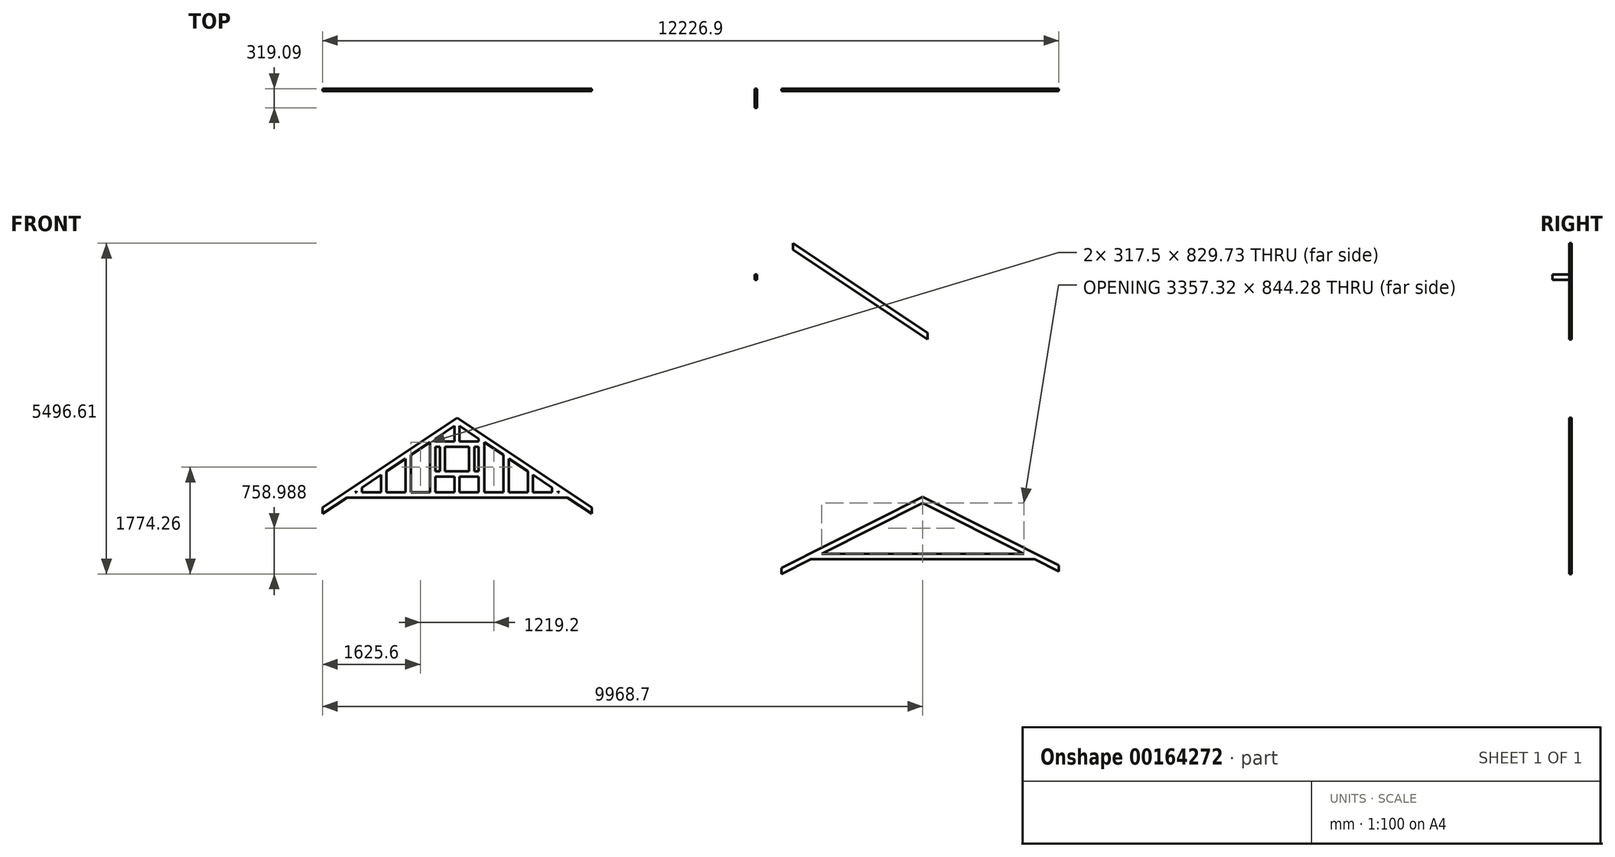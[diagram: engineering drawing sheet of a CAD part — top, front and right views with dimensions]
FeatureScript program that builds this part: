
annotation { "Feature Type Name" : "Feature", "Feature Type Description" : "" }
export const myFeature = defineFeature(function(context is Context, id is Id, definition is map)
    precondition{}
    {
        {
            var Q0;
            Q0=qCreatedBy(makeId("Front.planeOp"),FACE);
            var sketch = newSketch(context, id + "F0", { "sketchPlane" : qUnion([Q0])});
            skLineSegment(sketch, "E0.bottom", {"start": v(-99.94, 105.79) * mm, "end": v(3610.9, 105.79) * mm});
            skLineSegment(sketch, "E1", {"start": v(-592.94, -142.16) * mm, "end": v(-99.94, 105.79) * mm});
            skLineSegment(sketch, "E2", {"start": v(4013.66, -96.78) * mm, "end": v(3610.9, 105.79) * mm});
            skLineSegment(sketch, "E3", {"start": v(1738.69, 194.69) * mm, "end": v(76.82, 194.69) * mm});
            skLineSegment(sketch, "E4", {"start": v(1738.69, 194.69) * mm, "end": v(3434.14, 194.69) * mm});
            skLineSegment(sketch, "E5", {"start": v(-592.94, -42.65) * mm, "end": v(1755.48, 1138.48) * mm});
            skLineSegment(sketch, "E6", {"start": v(4013.66, 2.73) * mm, "end": v(1755.48, 1138.48) * mm});
            skLineSegment(sketch, "E7", {"start": v(-99.94, 105.79) * mm, "end": v(-592.94, -142.16) * mm});
            skLineSegment(sketch, "E8", {"start": v(3610.9, 105.79) * mm, "end": v(4013.66, -96.78) * mm});
            skLineSegment(sketch, "E9", {"start": v(-592.94, -42.65) * mm, "end": v(-592.94, -142.16) * mm});
            skLineSegment(sketch, "E10", {"start": v(4013.66, 2.73) * mm, "end": v(4013.66, -96.78) * mm});
            skLineSegment(sketch, "E11.trimOffspring", {"start": v(76.82, 194.69) * mm, "end": v(1755.48, 1038.97) * mm});
            skLineSegment(sketch, "E12.trimOffspring", {"start": v(3434.14, 194.69) * mm, "end": v(1755.48, 1038.97) * mm});
            skSolve(sketch);
        }
        {
            var Q0;
            Q0 = qSketchRegion(id + "F0", true);
            extrude(context, id + "F1", {"entities" : qUnion([Q0]), "depth" : 38.1 * mm});
        }
        {
            var Q0;
            Q0=qCreatedBy(makeId("Front.planeOp"),FACE);
            var sketch = newSketch(context, id + "F2", { "sketchPlane" : qUnion([Q0])});
            skLineSegment(sketch, "E13.bottom", {"start": v(-7806.82, 1128.33) * mm, "end": v(-4149.22, 1128.33) * mm});
            skPoint(sketch, "E14.endSnap0", {"position": v(-5978.02, 1128.33) * mm});
            skLineSegment(sketch, "E15", {"start": v(-3742.82, 857.4) * mm, "end": v(-4149.22, 1128.33) * mm});
            skLineSegment(sketch, "E16", {"start": v(-6022.47, 1217.23) * mm, "end": v(-6339.97, 1217.23) * mm});
            skLineSegment(sketch, "E17", {"start": v(-5933.57, 1217.23) * mm, "end": v(-5616.07, 1217.23) * mm});
            skLineSegment(sketch, "E18", {"start": v(-8213.22, 964.24) * mm, "end": v(-5978.02, 2454.38) * mm});
            skLineSegment(sketch, "E19", {"start": v(-3742.82, 964.24) * mm, "end": v(-5978.02, 2454.38) * mm});
            skPoint(sketch, "E20.start.orphan", {"position": v(-6892.42, 1737.93) * mm});
            skPoint(sketch, "E21.start.orphan", {"position": v(-5063.62, 1737.93) * mm});
            skLineSegment(sketch, "E22", {"start": v(-7806.82, 1128.33) * mm, "end": v(-8213.22, 857.4) * mm});
            skLineSegment(sketch, "E23", {"start": v(-4149.22, 1128.33) * mm, "end": v(-3742.82, 857.4) * mm});
            skLineSegment(sketch, "E24.0", {"start": v(-5933.57, 1217.23) * mm, "end": v(-5933.57, 1475.46) * mm});
            skLineSegment(sketch, "E25.0", {"start": v(-6022.47, 1217.23) * mm, "end": v(-6022.47, 1475.46) * mm});
            skLineSegment(sketch, "E26.1.0.0", {"start": v(-6428.87, 1217.23) * mm, "end": v(-6428.87, 2046.96) * mm});
            skLineSegment(sketch, "E26.1.0.1", {"start": v(-6339.97, 1217.23) * mm, "end": v(-6339.97, 1475.46) * mm});
            skLineSegment(sketch, "E26.1.0.2", {"start": v(-6339.97, 1217.23) * mm, "end": v(-6022.47, 1217.23) * mm});
            skLineSegment(sketch, "E26.2.0.0", {"start": v(-6835.27, 1217.23) * mm, "end": v(-6835.27, 1776.03) * mm});
            skLineSegment(sketch, "E26.2.0.1", {"start": v(-6746.37, 1217.23) * mm, "end": v(-6746.37, 1835.3) * mm});
            skLineSegment(sketch, "E26.2.0.2", {"start": v(-6746.37, 1217.23) * mm, "end": v(-6428.87, 1217.23) * mm});
            skLineSegment(sketch, "E26.3.0.0", {"start": v(-7241.67, 1217.23) * mm, "end": v(-7241.67, 1505.1) * mm});
            skLineSegment(sketch, "E26.3.0.1", {"start": v(-7152.77, 1217.23) * mm, "end": v(-7152.77, 1564.36) * mm});
            skLineSegment(sketch, "E26.3.0.2", {"start": v(-7152.77, 1217.23) * mm, "end": v(-6835.27, 1217.23) * mm});
            skLineSegment(sketch, "E26.4.0.0", {"start": v(-7648.07, 1217.23) * mm, "end": v(-7648.07, 1234.16) * mm});
            skLineSegment(sketch, "E26.4.0.1", {"start": v(-7559.17, 1217.23) * mm, "end": v(-7559.17, 1293.43) * mm});
            skLineSegment(sketch, "E26.4.0.2", {"start": v(-7559.17, 1217.23) * mm, "end": v(-7241.67, 1217.23) * mm});
            skLineSegment(sketch, "E27.1.0.0", {"start": v(-5616.07, 1217.23) * mm, "end": v(-5616.07, 1475.46) * mm});
            skLineSegment(sketch, "E27.1.0.1", {"start": v(-5527.17, 1217.23) * mm, "end": v(-5527.17, 2046.96) * mm});
            skLineSegment(sketch, "E27.2.0.0", {"start": v(-5209.67, 1217.23) * mm, "end": v(-5209.67, 1835.3) * mm});
            skLineSegment(sketch, "E27.2.0.1", {"start": v(-5120.77, 1217.23) * mm, "end": v(-5120.77, 1776.03) * mm});
            skLineSegment(sketch, "E27.3.0.0", {"start": v(-4803.27, 1217.23) * mm, "end": v(-4803.27, 1564.36) * mm});
            skLineSegment(sketch, "E27.3.0.1", {"start": v(-4714.37, 1217.23) * mm, "end": v(-4714.37, 1505.1) * mm});
            skLineSegment(sketch, "E27.4.0.0", {"start": v(-4396.87, 1217.23) * mm, "end": v(-4396.87, 1293.43) * mm});
            skLineSegment(sketch, "E27.4.0.1", {"start": v(-4307.97, 1217.23) * mm, "end": v(-4307.97, 1234.16) * mm});
            skPoint(sketch, "E28.orphan", {"position": v(-6022.47, 2347.53) * mm});
            skPoint(sketch, "E29.orphan", {"position": v(-5933.57, 2347.53) * mm});
            skLineSegment(sketch, "E30", {"start": v(-5616.07, 1970.76) * mm, "end": v(-5692.27, 1970.76) * mm});
            skLineSegment(sketch, "E31", {"start": v(-5616.07, 1767.56) * mm, "end": v(-5616.07, 1564.36) * mm});
            skLineSegment(sketch, "E32", {"start": v(-5616.07, 1564.36) * mm, "end": v(-5692.27, 1564.36) * mm});
            skLineSegment(sketch, "E33.0", {"start": v(-5616.07, 1475.46) * mm, "end": v(-5933.57, 1475.46) * mm});
            skLineSegment(sketch, "E34.0", {"start": v(-5616.07, 2059.66) * mm, "end": v(-6339.97, 2059.66) * mm});
            skLineSegment(sketch, "E35.trimOffspring", {"start": v(-5692.27, 1564.36) * mm, "end": v(-5692.27, 1970.76) * mm});
            skLineSegment(sketch, "E36.trimOffspring", {"start": v(-6263.77, 1564.36) * mm, "end": v(-6263.77, 1970.76) * mm});
            skLineSegment(sketch, "E37.trimOffspring", {"start": v(-5933.57, 2059.66) * mm, "end": v(-5933.57, 2317.9) * mm});
            skLineSegment(sketch, "E38.trimOffspring", {"start": v(-6022.47, 2059.66) * mm, "end": v(-6022.47, 2317.9) * mm});
            skLineSegment(sketch, "E39.trimOffspring", {"start": v(-6746.37, 1835.3) * mm, "end": v(-6428.87, 2046.96) * mm});
            skLineSegment(sketch, "E40.trimOffspring", {"start": v(-7152.77, 1564.36) * mm, "end": v(-6835.27, 1776.03) * mm});
            skLineSegment(sketch, "E41.trimOffspring", {"start": v(-7559.17, 1293.43) * mm, "end": v(-7241.67, 1505.1) * mm});
            skLineSegment(sketch, "E42.trimOffspring", {"start": v(-7648.07, 1217.23) * mm, "end": v(-7673.47, 1217.23) * mm});
            skLineSegment(sketch, "E43.trimOffspring", {"start": v(-7241.67, 1217.23) * mm, "end": v(-7559.17, 1217.23) * mm});
            skLineSegment(sketch, "E44.trimOffspring", {"start": v(-6835.27, 1217.23) * mm, "end": v(-7152.77, 1217.23) * mm});
            skLineSegment(sketch, "E45.trimOffspring", {"start": v(-6428.87, 1217.23) * mm, "end": v(-6746.37, 1217.23) * mm});
            skLineSegment(sketch, "E46.trimOffspring", {"start": v(-5933.57, 1217.23) * mm, "end": v(-5908.17, 1217.23) * mm});
            skLineSegment(sketch, "E47.trimOffspring", {"start": v(-6022.47, 1475.46) * mm, "end": v(-6339.97, 1475.46) * mm});
            skLineSegment(sketch, "E48.trimOffspring", {"start": v(-6263.77, 1564.36) * mm, "end": v(-6339.97, 1564.36) * mm});
            skLineSegment(sketch, "E49.trimOffspring", {"start": v(-5781.17, 1564.36) * mm, "end": v(-6174.87, 1564.36) * mm});
            skLineSegment(sketch, "E50.trimOffspring", {"start": v(-5616.07, 1564.36) * mm, "end": v(-5616.07, 1970.76) * mm});
            skLineSegment(sketch, "E51.trimOffspring", {"start": v(-6339.97, 1564.36) * mm, "end": v(-6339.97, 1970.76) * mm});
            skLineSegment(sketch, "E52.trimOffspring", {"start": v(-5527.17, 1217.23) * mm, "end": v(-5209.67, 1217.23) * mm});
            skLineSegment(sketch, "E53.trimOffspring", {"start": v(-5527.17, 1217.23) * mm, "end": v(-5501.77, 1217.23) * mm});
            skLineSegment(sketch, "E54.trimOffspring", {"start": v(-5120.77, 1217.23) * mm, "end": v(-4803.27, 1217.23) * mm});
            skLineSegment(sketch, "E55.trimOffspring", {"start": v(-5120.77, 1217.23) * mm, "end": v(-5095.37, 1217.23) * mm});
            skLineSegment(sketch, "E56.trimOffspring", {"start": v(-4714.37, 1217.23) * mm, "end": v(-4688.97, 1217.23) * mm});
            skLineSegment(sketch, "E57.trimOffspring", {"start": v(-4714.37, 1217.23) * mm, "end": v(-4396.87, 1217.23) * mm});
            skLineSegment(sketch, "E58.trimOffspring", {"start": v(-4307.97, 1217.23) * mm, "end": v(-4282.57, 1217.23) * mm});
            skLineSegment(sketch, "E59.trimOffspring", {"start": v(-4396.87, 1293.43) * mm, "end": v(-4714.37, 1505.1) * mm});
            skLineSegment(sketch, "E60.trimOffspring", {"start": v(-4282.57, 1217.23) * mm, "end": v(-4307.97, 1234.16) * mm});
            skLineSegment(sketch, "E61.trimOffspring", {"start": v(-5209.67, 1835.3) * mm, "end": v(-5527.17, 2046.96) * mm});
            skLineSegment(sketch, "E62.trimOffspring", {"start": v(-4803.27, 1564.36) * mm, "end": v(-5120.77, 1776.03) * mm});
            skLineSegment(sketch, "E63.trimOffspring", {"start": v(-5616.07, 2106.23) * mm, "end": v(-5933.57, 2317.9) * mm});
            skLineSegment(sketch, "E64.trimOffspring", {"start": v(-5616.07, 2059.66) * mm, "end": v(-5616.07, 2106.23) * mm});
            skLineSegment(sketch, "E65.trimOffspring", {"start": v(-6339.97, 2059.66) * mm, "end": v(-6339.97, 2106.23) * mm});
            skLineSegment(sketch, "E66.trimOffspring", {"start": v(-6263.77, 1970.76) * mm, "end": v(-6339.97, 1970.76) * mm});
            skLineSegment(sketch, "E67.trimOffspring", {"start": v(-5692.27, 1970.76) * mm, "end": v(-5616.07, 1970.76) * mm});
            skLineSegment(sketch, "E68.trimOffspring", {"start": v(-6339.97, 2106.23) * mm, "end": v(-6022.47, 2317.9) * mm});
            skLineSegment(sketch, "E69.trimOffspring", {"start": v(-7673.47, 1217.23) * mm, "end": v(-7648.07, 1234.16) * mm});
            skLineSegment(sketch, "E70.0", {"start": v(-6181.22, 1564.36) * mm, "end": v(-6181.22, 1970.76) * mm});
            skLineSegment(sketch, "E71.0", {"start": v(-5774.82, 1564.36) * mm, "end": v(-5774.82, 1970.76) * mm});
            skLineSegment(sketch, "E72", {"start": v(-6181.22, 1970.76) * mm, "end": v(-5774.82, 1970.76) * mm});
            skLineSegment(sketch, "E73.top", {"start": v(-6181.22, 1564.36) * mm, "end": v(-5774.82, 1564.36) * mm});
            skLineSegment(sketch, "E73.left", {"start": v(-6181.22, 1970.76) * mm, "end": v(-6181.22, 1564.36) * mm});
            skLineSegment(sketch, "E73.right", {"start": v(-5774.82, 1970.76) * mm, "end": v(-5774.82, 1564.36) * mm});
            skLineSegment(sketch, "E74", {"start": v(-3742.82, 964.24) * mm, "end": v(-3742.82, 857.4) * mm});
            skLineSegment(sketch, "E75", {"start": v(-8213.22, 964.24) * mm, "end": v(-8213.22, 857.4) * mm});
            skSolve(sketch);
        }
        {
            var Q0;
            {var subQ12=sQuery(id+"F2.wireOp",EDGE,"E13.bottom");Q0=makeQuery(id+"F2.imprint","IMPRINT",FACE,{"disambiguationData":[TD([[makeQuery(id+"F2.imprint","IMPRINT",EDGE,{"derivedFrom":subQ12}),1.0]])]});}
            extrude(context, id + "F3", {"entities" : qUnion([Q0]), "depth" : 38.1 * mm});
        }
        {
            var Q0;
            Q0=qCreatedBy(makeId("Front.planeOp"),FACE);
            var sketch = newSketch(context, id + "F4", { "sketchPlane" : qUnion([Q0])});
            skLineSegment(sketch, "E76", {"start": v(1832.31, 3757.47) * mm, "end": v(-402.88, 5247.6) * mm});
            skLineSegment(sketch, "E77", {"start": v(1832.31, 3864.31) * mm, "end": v(-402.88, 5354.45) * mm});
            skLineSegment(sketch, "E78", {"start": v(-402.88, 5247.6) * mm, "end": v(-402.88, 5354.45) * mm});
            skLineSegment(sketch, "E79", {"start": v(-402.88, 5247.6) * mm, "end": v(-353.57, 5321.57) * mm});
            skLineSegment(sketch, "E80.1.0.0", {"start": v(-64.74, 5022.17) * mm, "end": v(-15.43, 5096.14) * mm});
            skLineSegment(sketch, "E80.2.0.0", {"start": v(273.4, 4796.74) * mm, "end": v(322.72, 4870.71) * mm});
            skLineSegment(sketch, "E80.3.0.0", {"start": v(611.55, 4571.31) * mm, "end": v(660.86, 4645.28) * mm});
            skLineSegment(sketch, "E80.4.0.0", {"start": v(949.69, 4345.89) * mm, "end": v(999, 4419.85) * mm});
            skLineSegment(sketch, "E80.5.0.0", {"start": v(1287.83, 4120.46) * mm, "end": v(1337.15, 4194.43) * mm});
            skLineSegment(sketch, "E80.6.0.0", {"start": v(1625.98, 3895.03) * mm, "end": v(1675.29, 3969) * mm});
            skPoint(sketch, "E81.orphan", {"position": v(-277.47, 5435.72) * mm});
            skPoint(sketch, "E82.orphan", {"position": v(61.41, 5211.4) * mm});
            skPoint(sketch, "E83.orphan", {"position": v(400.3, 4987.09) * mm});
            skPoint(sketch, "E84.orphan", {"position": v(1078.07, 4538.46) * mm});
            skPoint(sketch, "E85.orphan", {"position": v(739.19, 4762.77) * mm});
            skPoint(sketch, "E86.orphan", {"position": v(1416.96, 4314.14) * mm});
            skPoint(sketch, "E87.orphan", {"position": v(1755.84, 4089.83) * mm});
            skPoint(sketch, "E88.orphan", {"position": v(1567.63, 3807.51) * mm});
            skPoint(sketch, "E89.orphan", {"position": v(1228.75, 4031.83) * mm});
            skPoint(sketch, "E90.orphan", {"position": v(889.86, 4256.14) * mm});
            skPoint(sketch, "E91.orphan", {"position": v(550.98, 4480.46) * mm});
            skPoint(sketch, "E92.orphan", {"position": v(212.09, 4704.77) * mm});
            skLineSegment(sketch, "E93", {"start": v(-402.88, 5354.45) * mm, "end": v(1832.31, 3864.31) * mm});
            skLineSegment(sketch, "E94", {"start": v(1832.31, 3864.31) * mm, "end": v(1832.31, 3757.47) * mm});
            skSolve(sketch);
        }
        {
            var Q0;
            Q0=qCreatedBy(makeId("Front.planeOp"),FACE);
            var sketch = newSketch(context, id + "F5", { "sketchPlane" : qUnion([Q0])});
            skLineSegment(sketch, "E95.bottom", {"start": v(-1033.12, 4833.83) * mm, "end": v(-995.02, 4833.83) * mm});
            skLineSegment(sketch, "E95.top", {"start": v(-1033.12, 4744.93) * mm, "end": v(-995.02, 4744.93) * mm});
            skLineSegment(sketch, "E95.left", {"start": v(-1033.12, 4833.83) * mm, "end": v(-1033.12, 4744.93) * mm});
            skLineSegment(sketch, "E95.right", {"start": v(-995.02, 4833.83) * mm, "end": v(-995.02, 4744.93) * mm});
            skSolve(sketch);
        }
        {
            var Q0;
            Q0 = qSketchRegion(id + "F5", true);
            extrude(context, id + "F6", {"entities" : qUnion([Q0]), "depth" : 319.09 * mm});
        }
        {
            var Q0;
            Q0 = qSketchRegion(id + "F4", true);
            extrude(context, id + "F7", {"entities" : qUnion([Q0]), "depth" : 38.1 * mm});
        }
        {
            var Q0;
            Q0=makeQuery(id+"F7.opExtrude","CAP_FACE",FACE,{"disambiguationData":[OSD([sQuery(id+"F4.wireOp",EDGE,"E76"),sQuery(id+"F4.wireOp",EDGE,"E77"),sQuery(id+"F4.wireOp",EDGE,"b436f2d1-3bbd-437f-b9da-59f5766fd485"),sQuery(id+"F4.wireOp",EDGE,"E78")])],"isStart":false});
            var sketch = newSketch(context, id + "F8", { "sketchPlane" : qUnion([Q0])});
            skLineSegment(sketch, "E96", {"start": v(-402.88, 5247.6) * mm, "end": v(-353.57, 5321.57) * mm});
            skLineSegment(sketch, "E97.1.0.0", {"start": v(-64.74, 5022.17) * mm, "end": v(-15.42, 5096.14) * mm});
            skLineSegment(sketch, "E97.2.0.0", {"start": v(273.4, 4796.75) * mm, "end": v(322.72, 4870.71) * mm});
            skLineSegment(sketch, "E97.3.0.0", {"start": v(611.56, 4571.32) * mm, "end": v(660.87, 4645.29) * mm});
            skLineSegment(sketch, "E97.4.0.0", {"start": v(949.7, 4345.9) * mm, "end": v(999.02, 4419.86) * mm});
            skLineSegment(sketch, "E97.5.0.0", {"start": v(1287.85, 4120.46) * mm, "end": v(1337.16, 4194.43) * mm});
            skLineSegment(sketch, "E97.6.0.0", {"start": v(1626, 3895.03) * mm, "end": v(1675.3, 3969) * mm});
            skSolve(sketch);
        }
    });
